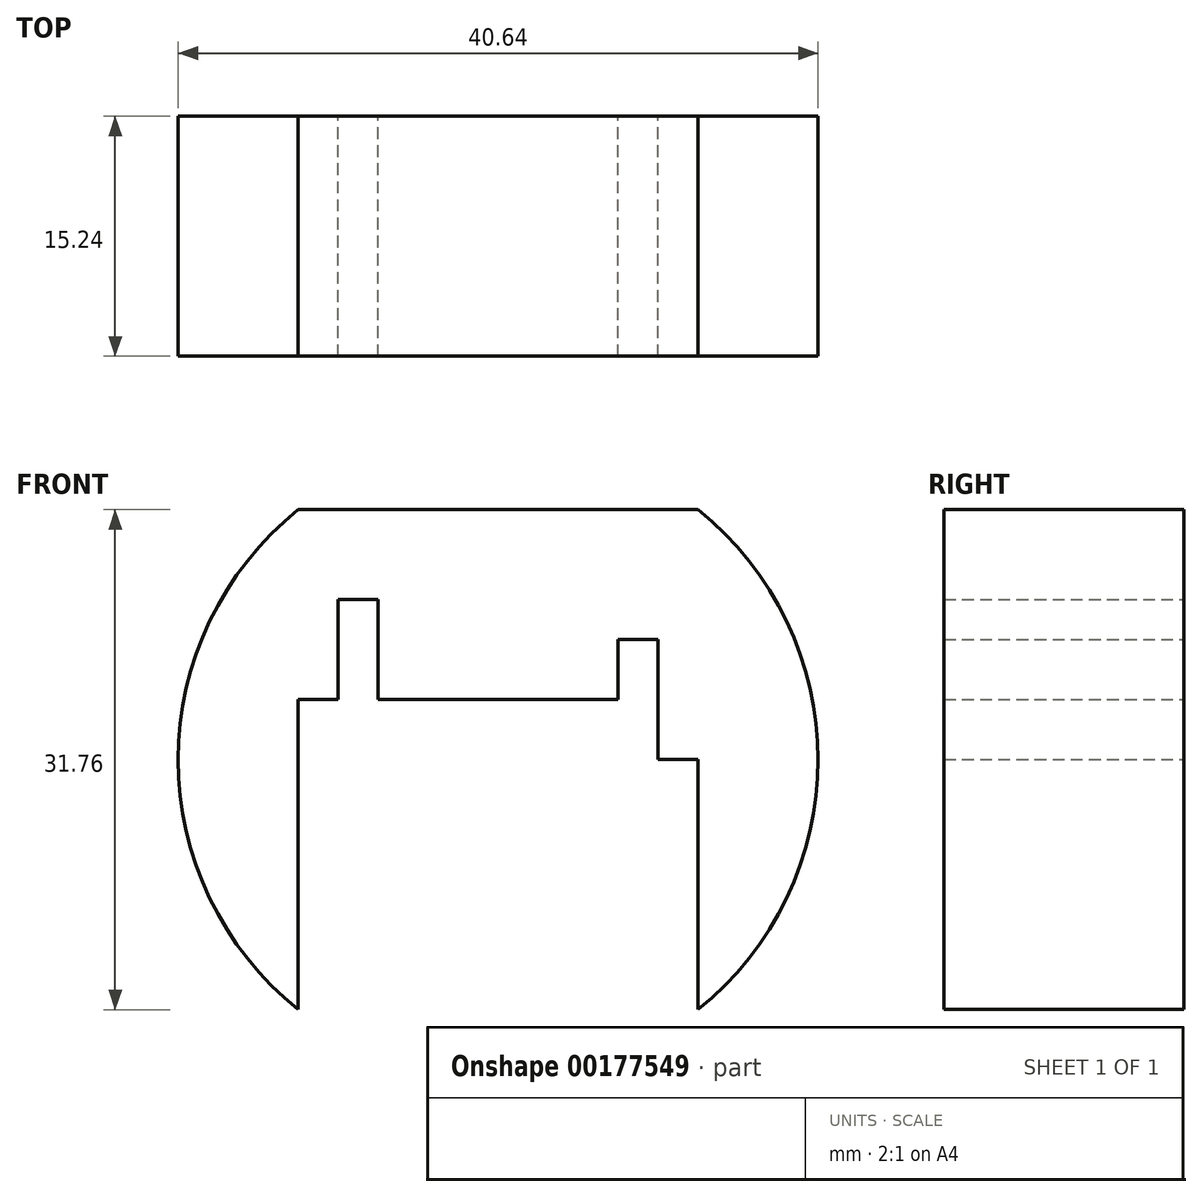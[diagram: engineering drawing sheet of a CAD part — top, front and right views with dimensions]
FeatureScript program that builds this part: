
annotation { "Feature Type Name" : "Feature", "Feature Type Description" : "" }
export const myFeature = defineFeature(function(context is Context, id is Id, definition is map)
    precondition{}
    {
        {
            var Q0;
            Q0=qCreatedBy(makeId("Front.planeOp"),FACE);
            var sketch = newSketch(context, id + "F0", { "sketchPlane" : qUnion([Q0])});
            skLineSegment(sketch, "E0.bottom", {"start": v(12.7, 15.88) * mm, "end": v(-12.7, 15.88) * mm});
            skLineSegment(sketch, "E0.top", {"start": v(12.7, -15.88) * mm, "end": v(-12.7, -15.88) * mm});
            skLineSegment(sketch, "E0.left", {"start": v(12.7, 15.88) * mm, "end": v(12.7, -15.88) * mm});
            skLineSegment(sketch, "E0.right", {"start": v(-12.7, 15.88) * mm, "end": v(-12.7, -15.88) * mm});
            skPoint(sketch, "E0.middle", {"position": v(0, 0) * mm});
            skLineSegment(sketch, "E1", {"start": v(-12.7, 0) * mm, "end": v(-20.32, 0) * mm});
            skLineSegment(sketch, "E2", {"start": v(12.7, 0) * mm, "end": v(20.32, 0) * mm});
            skPoint(sketch, "E2.endSnap0", {"position": v(12.7, 0) * mm});
            skArc(sketch, "E3", {"start": v(-12.7, 15.88) * mm, "mid": v(-20.32, 0) * mm, "end": v(-12.7, -15.88) * mm});
            skArc(sketch, "E4", {"start": v(12.7, -15.88) * mm, "mid": v(20.32, 0) * mm, "end": v(12.7, 15.88) * mm});
            skLineSegment(sketch, "E5", {"start": v(0, -15.88) * mm, "end": v(0, -13.33) * mm});
            skLineSegment(sketch, "E6", {"start": v(0, -13.33) * mm, "end": v(3.17, -13.33) * mm});
            skLineSegment(sketch, "E7", {"start": v(3.17, -13.33) * mm, "end": v(0, -13.33) * mm});
            skLineSegment(sketch, "E8", {"start": v(0, -13.33) * mm, "end": v(-3.18, -13.33) * mm});
            skLineSegment(sketch, "E9", {"start": v(-3.18, -13.33) * mm, "end": v(-3.18, -6.98) * mm});
            skLineSegment(sketch, "E10", {"start": v(3.17, -13.33) * mm, "end": v(3.17, -6.98) * mm});
            skArc(sketch, "E11", {"start": v(-3.18, -6.98) * mm, "mid": v(0, -3.8) * mm, "end": v(3.17, -6.98) * mm});
            skLineSegment(sketch, "E12", {"start": v(12.7, 0) * mm, "end": v(10.16, 0) * mm});
            skLineSegment(sketch, "E13", {"start": v(10.16, 0) * mm, "end": v(10.16, 7.62) * mm});
            skLineSegment(sketch, "E14", {"start": v(10.16, 7.62) * mm, "end": v(7.62, 7.62) * mm});
            skLineSegment(sketch, "E15.bottom", {"start": v(10.16, 0) * mm, "end": v(7.62, 0) * mm});
            skLineSegment(sketch, "E15.right", {"start": v(7.62, 0) * mm, "end": v(7.62, 7.62) * mm});
            skLineSegment(sketch, "E16", {"start": v(7.62, 3.81) * mm, "end": v(-12.7, 3.81) * mm});
            skLineSegment(sketch, "E17", {"start": v(-12.7, 3.81) * mm, "end": v(-12.7, 0) * mm});
            skLineSegment(sketch, "E18", {"start": v(-12.7, 0) * mm, "end": v(-10.16, 0) * mm});
            skLineSegment(sketch, "E19", {"start": v(-10.16, 3.81) * mm, "end": v(-10.16, 10.16) * mm});
            skLineSegment(sketch, "E20", {"start": v(-10.16, 10.16) * mm, "end": v(-7.62, 10.16) * mm});
            skLineSegment(sketch, "E21", {"start": v(-7.62, 10.16) * mm, "end": v(-7.62, -2.54) * mm});
            skLineSegment(sketch, "E22.top", {"start": v(-10.16, -2.54) * mm, "end": v(-7.62, -2.54) * mm});
            skLineSegment(sketch, "E22.left", {"start": v(-10.16, 10.16) * mm, "end": v(-10.16, -2.54) * mm});
            skSolve(sketch);
        }
        {
            var Q0;
            {var subQ11=sQuery(id+"F0.wireOp",EDGE,"E0.bottom");Q0=makeQuery(id+"F0.imprint","IMPRINT",FACE,{"disambiguationData":[TD([[makeQuery(id+"F0.imprint","IMPRINT",EDGE,{"derivedFrom":subQ11}),1.0]])]});}
            var Q1;
            {var subQ3=sQuery(id+"F0.wireOp",EDGE,"E2");Q1=makeQuery(id+"F0.imprint","IMPRINT",FACE,{"disambiguationData":[TD([[makeQuery(id+"F0.imprint","IMPRINT",EDGE,{"derivedFrom":subQ3}),1.0]])]});}
            var Q2;
            Q2=makeQuery(id+"F0.imprint","IMPRINT",FACE,{"disambiguationData":[TD([[makeQuery(id+"F0.imprint","IMPRINT",EDGE,{"derivedFrom":sQuery(id+"F0.wireOp",EDGE,"E7")}),1.0]])]});
            var Q3;
            {var subQ3=sQuery(id+"F0.wireOp",EDGE,"E2");Q3=makeQuery(id+"F0.imprint","IMPRINT",FACE,{"disambiguationData":[TD([[makeQuery(id+"F0.imprint","IMPRINT",EDGE,{"derivedFrom":subQ3}),-1.0]])]});}
            var Q4;
            {var subQ0=sQuery(id+"F0.wireOp",EDGE,"E17");Q4=makeQuery(id+"F0.imprint","IMPRINT",FACE,{"disambiguationData":[TD([[makeQuery(id+"F0.imprint","IMPRINT",EDGE,{"derivedFrom":subQ0}),1.0]])]});}
            var Q5;
            {var subQ4=sQuery(id+"F0.wireOp",EDGE,"E1");Q5=makeQuery(id+"F0.imprint","IMPRINT",FACE,{"disambiguationData":[TD([[makeQuery(id+"F0.imprint","IMPRINT",EDGE,{"derivedFrom":subQ4}),-1.0]])]});}
            var Q6;
            {var subQ3=sQuery(id+"F0.wireOp",EDGE,"E1");Q6=makeQuery(id+"F0.imprint","IMPRINT",FACE,{"disambiguationData":[TD([[makeQuery(id+"F0.imprint","IMPRINT",EDGE,{"derivedFrom":subQ3}),1.0]])]});}
            extrude(context, id + "F1", {"entities" : qUnion([Q0, Q1, Q2, Q3, Q4, Q5, Q6]), "depth" : 15.24 * mm});
        }
    });
